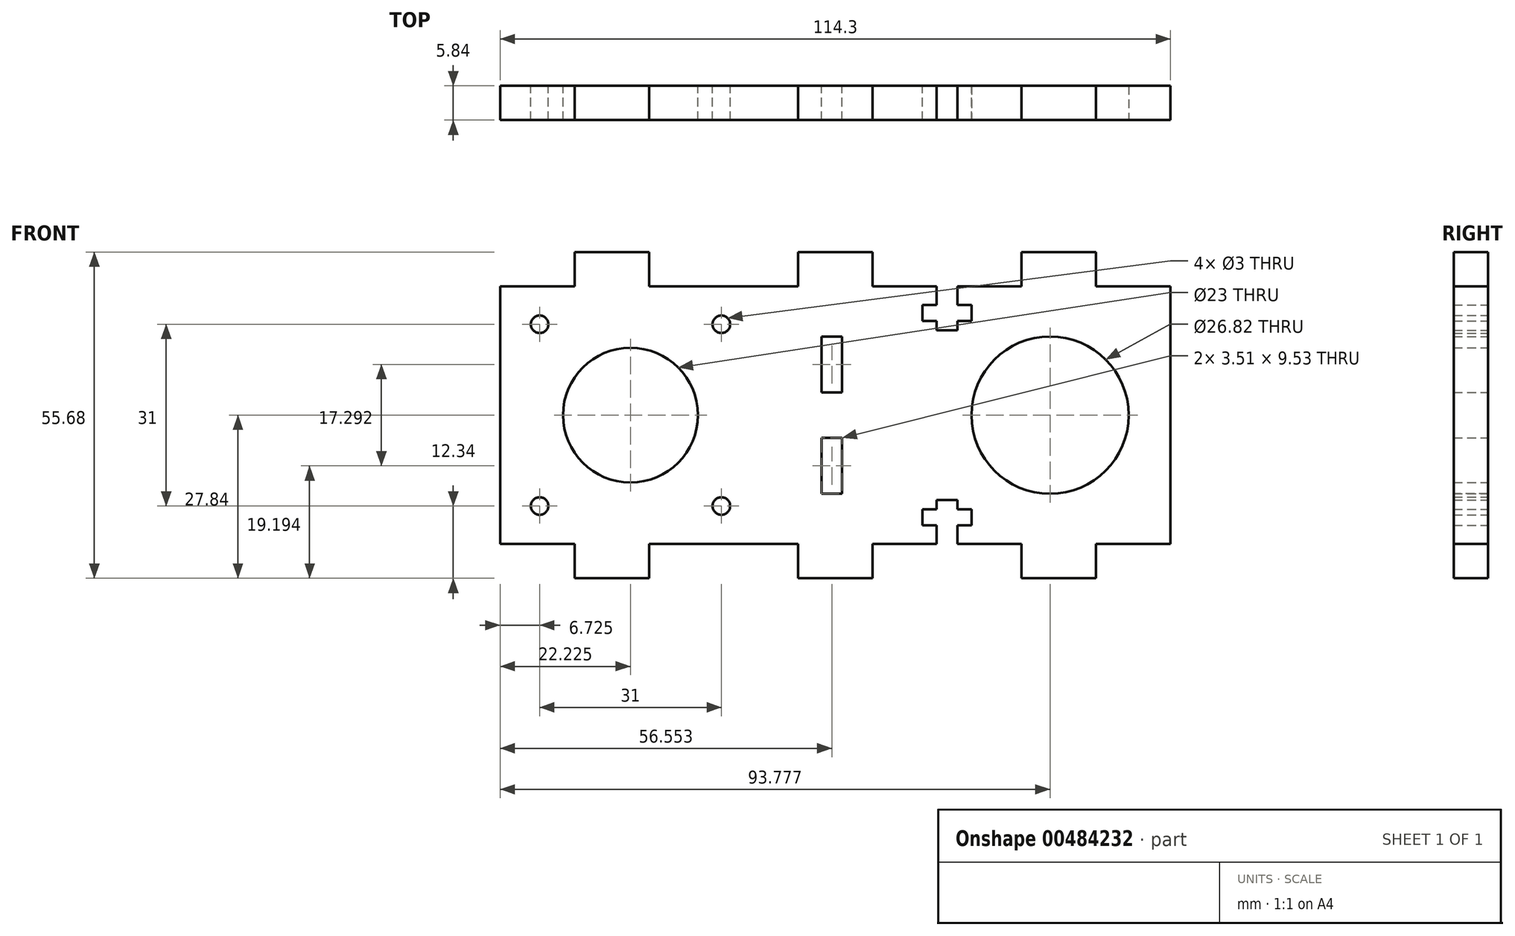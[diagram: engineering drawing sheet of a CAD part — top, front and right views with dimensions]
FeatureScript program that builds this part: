
annotation { "Feature Type Name" : "Feature", "Feature Type Description" : "" }
export const myFeature = defineFeature(function(context is Context, id is Id, definition is map)
    precondition{}
    {
        {
            var Q0;
            Q0=qCreatedBy(makeId("Front.planeOp"),FACE);
            var sketch = newSketch(context, id + "F0", { "sketchPlane" : qUnion([Q0])});
            skLineSegment(sketch, "E0.bottom", {"start": v(-57.15, 22) * mm, "end": v(-44.45, 22) * mm});
            skLineSegment(sketch, "E0.left", {"start": v(-57.15, 22) * mm, "end": v(-57.15, -22) * mm});
            skLineSegment(sketch, "E0.right", {"start": v(57.15, 22) * mm, "end": v(57.15, -22) * mm});
            skPoint(sketch, "E0.middle", {"position": v(0, 0) * mm});
            skCircle(sketch, "E1", {"center": v(-34.93, 0) * mm, "radius": 11.5 * mm});
            skCircle(sketch, "E2", {"center": v(36.63, 0) * mm, "radius": 10.86 * mm});
            skCircle(sketch, "E3", {"center": v(-50.43, 15.5) * mm, "radius": 1.5 * mm});
            skLineSegment(sketch, "E4", {"start": v(-34.93, 0) * mm, "end": v(-34.93, 11.5) * mm, "construction": true});
            skLineSegment(sketch, "E5", {"start": v(-34.93, 0) * mm, "end": v(-46.43, 0) * mm, "construction": true});
            skCircle(sketch, "E6.MirrorC", {"center": v(-19.43, 15.5) * mm, "radius": 1.5 * mm});
            skCircle(sketch, "E7.MirrorC", {"center": v(-19.43, -15.5) * mm, "radius": 1.5 * mm});
            skCircle(sketch, "E8.MirrorC", {"center": v(-50.43, -15.5) * mm, "radius": 1.5 * mm});
            skCircle(sketch, "E9", {"center": v(-34.93, 0) * mm, "radius": 5 * mm, "construction": true});
            skCircle(sketch, "E10", {"center": v(36.63, 0) * mm, "radius": 12.5 * mm, "construction": true});
            skLineSegment(sketch, "E11", {"start": v(-35.45, 4.97) * mm, "end": v(35.32, 12.43) * mm, "construction": true});
            skLineSegment(sketch, "E12.MirrorCS", {"start": v(-35.45, -4.97) * mm, "end": v(35.32, -12.43) * mm, "construction": true});
            skLineSegment(sketch, "E13", {"start": v(-0.6, 0) * mm, "end": v(-0.6, 12.84) * mm, "construction": true});
            skLineSegment(sketch, "E14.bottom", {"start": v(1.16, 13.4) * mm, "end": v(-2.35, 13.4) * mm});
            skLineSegment(sketch, "E14.top", {"start": v(1.16, 3.88) * mm, "end": v(-2.35, 3.88) * mm});
            skLineSegment(sketch, "E14.left", {"start": v(1.16, 13.4) * mm, "end": v(1.16, 3.88) * mm});
            skLineSegment(sketch, "E14.right", {"start": v(-2.35, 13.4) * mm, "end": v(-2.35, 3.88) * mm});
            skPoint(sketch, "E14.middle", {"position": v(-0.6, 8.65) * mm});
            skLineSegment(sketch, "E15.MirrorCS", {"start": v(1.16, -13.4) * mm, "end": v(-2.35, -13.4) * mm});
            skPoint(sketch, "E16.MirrorP", {"position": v(-0.6, -8.65) * mm});
            skLineSegment(sketch, "E17.MirrorCS", {"start": v(1.16, -13.4) * mm, "end": v(1.16, -3.88) * mm});
            skLineSegment(sketch, "E18.MirrorCS", {"start": v(1.16, -3.88) * mm, "end": v(-2.35, -3.88) * mm});
            skLineSegment(sketch, "E19.MirrorCS", {"start": v(-2.35, -13.4) * mm, "end": v(-2.35, -3.88) * mm});
            skLineSegment(sketch, "E20.top", {"start": v(-44.45, 27.84) * mm, "end": v(-31.75, 27.84) * mm});
            skLineSegment(sketch, "E20.left", {"start": v(-44.45, 22) * mm, "end": v(-44.45, 27.84) * mm});
            skLineSegment(sketch, "E20.right", {"start": v(-31.75, 22) * mm, "end": v(-31.75, 27.84) * mm});
            skPoint(sketch, "E20.middle", {"position": v(-38.1, 24.92) * mm});
            skLineSegment(sketch, "E21.trimOffspring", {"start": v(-31.75, 22) * mm, "end": v(-20.8, 22) * mm});
            skLineSegment(sketch, "E22.MirrorCS", {"start": v(44.45, 27.84) * mm, "end": v(31.75, 27.84) * mm});
            skLineSegment(sketch, "E23.MirrorCS", {"start": v(31.75, 22) * mm, "end": v(31.75, 27.84) * mm});
            skLineSegment(sketch, "E24.MirrorCS", {"start": v(44.45, 22) * mm, "end": v(44.45, 27.84) * mm});
            skPoint(sketch, "E25.MirrorP", {"position": v(38.1, 24.92) * mm});
            skLineSegment(sketch, "E26.MirrorCS", {"start": v(44.45, -22) * mm, "end": v(44.45, -27.84) * mm});
            skLineSegment(sketch, "E27.MirrorCS", {"start": v(-44.45, -27.84) * mm, "end": v(-31.75, -27.84) * mm});
            skLineSegment(sketch, "E28.MirrorCS", {"start": v(31.75, -22) * mm, "end": v(31.75, -27.84) * mm});
            skPoint(sketch, "E29.MirrorP", {"position": v(38.1, -24.92) * mm});
            skLineSegment(sketch, "E30.MirrorCS", {"start": v(44.45, -27.84) * mm, "end": v(31.75, -27.84) * mm});
            skPoint(sketch, "E31.MirrorP", {"position": v(-38.1, -24.92) * mm});
            skLineSegment(sketch, "E32.MirrorCS", {"start": v(-31.75, -22) * mm, "end": v(-31.75, -27.84) * mm});
            skLineSegment(sketch, "E33.MirrorCS", {"start": v(-44.45, -22) * mm, "end": v(-44.45, -27.84) * mm});
            skLineSegment(sketch, "E34.trimOffspring", {"start": v(-31.75, -22) * mm, "end": v(-20.8, -22) * mm});
            skLineSegment(sketch, "E35.trimOffspring", {"start": v(44.45, -22) * mm, "end": v(57.15, -22) * mm});
            skLineSegment(sketch, "E36.trimOffspring", {"start": v(44.45, 22) * mm, "end": v(57.15, 22) * mm});
            skLineSegment(sketch, "E37", {"start": v(-57.15, -22) * mm, "end": v(-44.45, -22) * mm});
            skLineSegment(sketch, "E38.top", {"start": v(-6.35, 27.84) * mm, "end": v(6.35, 27.84) * mm});
            skLineSegment(sketch, "E38.left", {"start": v(-6.35, 22) * mm, "end": v(-6.35, 27.84) * mm});
            skLineSegment(sketch, "E38.right", {"start": v(6.35, 22) * mm, "end": v(6.35, 27.84) * mm});
            skPoint(sketch, "E38.middle", {"position": v(0, 24.92) * mm});
            skLineSegment(sketch, "E39.trimOffspring", {"start": v(6.35, 22) * mm, "end": v(17.3, 22) * mm});
            skLineSegment(sketch, "E40.MirrorCS", {"start": v(6.35, -22) * mm, "end": v(6.35, -27.84) * mm});
            skPoint(sketch, "E41.MirrorP", {"position": v(0, -24.92) * mm});
            skLineSegment(sketch, "E42.MirrorCS", {"start": v(-6.35, -22) * mm, "end": v(-6.35, -27.84) * mm});
            skLineSegment(sketch, "E43.MirrorCS", {"start": v(-6.35, -27.84) * mm, "end": v(6.35, -27.84) * mm});
            skLineSegment(sketch, "E44.trimOffspring", {"start": v(6.35, -22) * mm, "end": v(17.3, -22) * mm});
            skLineSegment(sketch, "E45", {"start": v(-19.05, 22) * mm, "end": v(-19.05, -22) * mm, "construction": true});
            skPoint(sketch, "E46.middle", {"position": v(-19.05, -20.41) * mm});
            skPoint(sketch, "E47.middle", {"position": v(-19.05, -17.44) * mm});
            skPoint(sketch, "E48.middle", {"position": v(-19.05, -15.25) * mm});
            skLineSegment(sketch, "E49", {"start": v(-20.82, -16.05) * mm, "end": v(-20.8, -16.05) * mm});
            skLineSegment(sketch, "E50.trimOffspring", {"start": v(-17.3, -22) * mm, "end": v(-6.35, -22) * mm});
            skPoint(sketch, "E51.MirrorP", {"position": v(19.05, -15.25) * mm});
            skLineSegment(sketch, "E52.MirrorCS", {"start": v(17.3, -16.05) * mm, "end": v(17.3, -14.46) * mm});
            skLineSegment(sketch, "E53.MirrorCS", {"start": v(23.22, -18.83) * mm, "end": v(20.8, -18.83) * mm});
            skLineSegment(sketch, "E54.MirrorCS", {"start": v(17.3, -16.05) * mm, "end": v(14.88, -16.05) * mm});
            skLineSegment(sketch, "E55.MirrorCS", {"start": v(14.88, -18.83) * mm, "end": v(14.88, -16.05) * mm});
            skPoint(sketch, "E56.MirrorP", {"position": v(19.05, -17.44) * mm});
            skPoint(sketch, "E57.MirrorP", {"position": v(19.05, -20.41) * mm});
            skLineSegment(sketch, "E58.MirrorCS", {"start": v(20.8, -16.05) * mm, "end": v(20.8, -14.46) * mm});
            skLineSegment(sketch, "E59.MirrorCS", {"start": v(23.22, -18.83) * mm, "end": v(23.22, -16.05) * mm});
            skLineSegment(sketch, "E60.MirrorCS", {"start": v(23.22, -16.05) * mm, "end": v(20.8, -16.05) * mm});
            skLineSegment(sketch, "E61.MirrorCS", {"start": v(20.8, -14.46) * mm, "end": v(17.3, -14.46) * mm});
            skLineSegment(sketch, "E62.MirrorCS", {"start": v(20.8, -22) * mm, "end": v(20.8, -18.83) * mm});
            skLineSegment(sketch, "E63.MirrorCS", {"start": v(17.3, -18.83) * mm, "end": v(14.88, -18.83) * mm});
            skLineSegment(sketch, "E64.MirrorCS", {"start": v(17.3, -22) * mm, "end": v(17.3, -18.83) * mm});
            skLineSegment(sketch, "E65.trimOffspring", {"start": v(20.8, -22) * mm, "end": v(31.75, -22) * mm});
            skLineSegment(sketch, "E66.MirrorCS", {"start": v(23.22, 16.05) * mm, "end": v(20.8, 16.05) * mm});
            skLineSegment(sketch, "E67.MirrorCS", {"start": v(17.3, 18.83) * mm, "end": v(14.88, 18.83) * mm});
            skLineSegment(sketch, "E68.MirrorCS", {"start": v(23.22, 18.83) * mm, "end": v(20.8, 18.83) * mm});
            skLineSegment(sketch, "E69.MirrorCS", {"start": v(17.3, 16.05) * mm, "end": v(17.3, 14.46) * mm});
            skLineSegment(sketch, "E70.MirrorCS", {"start": v(17.3, 16.05) * mm, "end": v(14.88, 16.05) * mm});
            skLineSegment(sketch, "E71.MirrorCS", {"start": v(20.8, 16.05) * mm, "end": v(20.8, 14.46) * mm});
            skLineSegment(sketch, "E72.MirrorCS", {"start": v(-20.82, 16.05) * mm, "end": v(-20.8, 16.05) * mm});
            skLineSegment(sketch, "E73.MirrorCS", {"start": v(20.8, 14.46) * mm, "end": v(17.3, 14.46) * mm});
            skPoint(sketch, "E74.MirrorP", {"position": v(19.05, 20.41) * mm});
            skLineSegment(sketch, "E75.MirrorCS", {"start": v(14.88, 18.83) * mm, "end": v(14.88, 16.05) * mm});
            skPoint(sketch, "E76.MirrorP", {"position": v(-19.05, 20.41) * mm});
            skLineSegment(sketch, "E77.MirrorCS", {"start": v(23.22, 18.83) * mm, "end": v(23.22, 16.05) * mm});
            skLineSegment(sketch, "E78.MirrorCS", {"start": v(-17.3, 22) * mm, "end": v(-6.35, 22) * mm});
            skLineSegment(sketch, "E79.MirrorCS", {"start": v(20.8, 22) * mm, "end": v(20.8, 18.83) * mm});
            skPoint(sketch, "E80.MirrorP", {"position": v(19.05, 15.25) * mm});
            skLineSegment(sketch, "E81.MirrorCS", {"start": v(17.3, 22) * mm, "end": v(17.3, 18.83) * mm});
            skPoint(sketch, "E82.MirrorP", {"position": v(-19.05, 15.25) * mm});
            skPoint(sketch, "E83.MirrorP", {"position": v(-19.05, 17.44) * mm});
            skPoint(sketch, "E84.MirrorP", {"position": v(19.05, 17.44) * mm});
            skLineSegment(sketch, "E85.trimOffspring", {"start": v(20.8, 22) * mm, "end": v(31.75, 22) * mm});
            skLineSegment(sketch, "E86", {"start": v(-20.8, -22) * mm, "end": v(-17.3, -22) * mm});
            skLineSegment(sketch, "E87", {"start": v(-20.8, 22) * mm, "end": v(-17.3, 22) * mm});
            skPoint(sketch, "E88.orphan", {"position": v(-20.8, 14.46) * mm});
            skPoint(sketch, "E89.MirrorCS.end.orphan", {"position": v(-23.22, 16.05) * mm});
            skPoint(sketch, "E90.MirrorCS.end.orphan", {"position": v(-20.8, 18.83) * mm});
            skPoint(sketch, "E90.MirrorCS.start.orphan", {"position": v(-23.22, 18.83) * mm});
            skPoint(sketch, "E91.MirrorCS.start.orphan", {"position": v(-17.3, 18.83) * mm});
            skPoint(sketch, "E92.MirrorCS.start.orphan", {"position": v(-14.88, 18.83) * mm});
            skPoint(sketch, "E93.MirrorCS.end.orphan", {"position": v(-14.88, 16.05) * mm});
            skPoint(sketch, "E94.MirrorCS.end.orphan", {"position": v(-17.3, 14.46) * mm});
            skPoint(sketch, "E94.MirrorCS.start.orphan", {"position": v(-17.3, 16.05) * mm});
            skPoint(sketch, "E95.orphan", {"position": v(-20.8, -14.46) * mm});
            skPoint(sketch, "E48.right.end.orphan", {"position": v(-17.3, -14.46) * mm});
            skPoint(sketch, "E96.trimOffspring.start.orphan", {"position": v(-17.3, -16.05) * mm});
            skPoint(sketch, "E47.right.end.orphan", {"position": v(-14.88, -16.05) * mm});
            skPoint(sketch, "E97.trimOffspring.end.orphan", {"position": v(-14.88, -18.83) * mm});
            skPoint(sketch, "E46.right.end.orphan", {"position": v(-17.3, -18.83) * mm});
            skPoint(sketch, "E98.end.orphan", {"position": v(-20.8, -18.83) * mm});
            skPoint(sketch, "E47.left.start.orphan", {"position": v(-23.22, -18.83) * mm});
            skPoint(sketch, "E99.orphan", {"position": v(-23.22, -16.05) * mm});
            skSolve(sketch);
        }
        {
            var Q0;
            Q0=qSketchRegion(id+"F0",true);
            extrude(context, id + "F1", {"entities" : qUnion([Q0]), "depth" : 5.84 * mm});
        }
        {
            var Q0;
            Q0=makeQuery(id+"F1.opExtrude","CAP_FACE",FACE,{"disambiguationData":[OSD([sQuery(id+"F0.wireOp",EDGE,"E0.bottom"),sQuery(id+"F0.wireOp",EDGE,"E0.left"),sQuery(id+"F0.wireOp",EDGE,"E0.right"),sQuery(id+"F0.wireOp",EDGE,"E1"),sQuery(id+"F0.wireOp",EDGE,"E2"),sQuery(id+"F0.wireOp",EDGE,"E3"),sQuery(id+"F0.wireOp",EDGE,"E7.MirrorC"),sQuery(id+"F0.wireOp",EDGE,"E8.MirrorC"),sQuery(id+"F0.wireOp",EDGE,"E14.top"),sQuery(id+"F0.wireOp",EDGE,"E14.left"),sQuery(id+"F0.wireOp",EDGE,"E14.right"),sQuery(id+"F0.wireOp",EDGE,"E15.MirrorCS"),sQuery(id+"F0.wireOp",EDGE,"E17.MirrorCS"),sQuery(id+"F0.wireOp",EDGE,"E18.MirrorCS"),sQuery(id+"F0.wireOp",EDGE,"E19.MirrorCS"),sQuery(id+"F0.wireOp",EDGE,"E20.top"),sQuery(id+"F0.wireOp",EDGE,"E20.left"),sQuery(id+"F0.wireOp",EDGE,"E20.right"),sQuery(id+"F0.wireOp",EDGE,"E21.trimOffspring"),sQuery(id+"F0.wireOp",EDGE,"E22.MirrorCS"),sQuery(id+"F0.wireOp",EDGE,"E23.MirrorCS"),sQuery(id+"F0.wireOp",EDGE,"E24.MirrorCS"),sQuery(id+"F0.wireOp",EDGE,"E26.MirrorCS"),sQuery(id+"F0.wireOp",EDGE,"E27.MirrorCS"),sQuery(id+"F0.wireOp",EDGE,"E28.MirrorCS"),sQuery(id+"F0.wireOp",EDGE,"E30.MirrorCS"),sQuery(id+"F0.wireOp",EDGE,"E32.MirrorCS"),sQuery(id+"F0.wireOp",EDGE,"E33.MirrorCS"),sQuery(id+"F0.wireOp",EDGE,"E34.trimOffspring"),sQuery(id+"F0.wireOp",EDGE,"E35.trimOffspring"),sQuery(id+"F0.wireOp",EDGE,"E36.trimOffspring"),sQuery(id+"F0.wireOp",EDGE,"E37"),sQuery(id+"F0.wireOp",EDGE,"E38.top"),sQuery(id+"F0.wireOp",EDGE,"E38.left"),sQuery(id+"F0.wireOp",EDGE,"E38.right"),sQuery(id+"F0.wireOp",EDGE,"E40.MirrorCS"),sQuery(id+"F0.wireOp",EDGE,"E42.MirrorCS"),sQuery(id+"F0.wireOp",EDGE,"E43.MirrorCS"),sQuery(id+"F0.wireOp",EDGE,"E44.trimOffspring"),sQuery(id+"F0.wireOp",EDGE,"E50.trimOffspring"),sQuery(id+"F0.wireOp",EDGE,"E52.MirrorCS"),sQuery(id+"F0.wireOp",EDGE,"E53.MirrorCS"),sQuery(id+"F0.wireOp",EDGE,"E54.MirrorCS"),sQuery(id+"F0.wireOp",EDGE,"E55.MirrorCS"),sQuery(id+"F0.wireOp",EDGE,"E58.MirrorCS"),sQuery(id+"F0.wireOp",EDGE,"E59.MirrorCS"),sQuery(id+"F0.wireOp",EDGE,"E60.MirrorCS"),sQuery(id+"F0.wireOp",EDGE,"E61.MirrorCS"),sQuery(id+"F0.wireOp",EDGE,"E62.MirrorCS"),sQuery(id+"F0.wireOp",EDGE,"E63.MirrorCS"),sQuery(id+"F0.wireOp",EDGE,"E64.MirrorCS"),sQuery(id+"F0.wireOp",EDGE,"E65.trimOffspring"),sQuery(id+"F0.wireOp",EDGE,"E66.MirrorCS"),sQuery(id+"F0.wireOp",EDGE,"E67.MirrorCS"),sQuery(id+"F0.wireOp",EDGE,"E68.MirrorCS"),sQuery(id+"F0.wireOp",EDGE,"E69.MirrorCS"),sQuery(id+"F0.wireOp",EDGE,"E70.MirrorCS"),sQuery(id+"F0.wireOp",EDGE,"E71.MirrorCS"),sQuery(id+"F0.wireOp",EDGE,"E73.MirrorCS"),sQuery(id+"F0.wireOp",EDGE,"E14.bottom"),sQuery(id+"F0.wireOp",EDGE,"E39.trimOffspring"),sQuery(id+"F0.wireOp",EDGE,"E75.MirrorCS"),sQuery(id+"F0.wireOp",EDGE,"E77.MirrorCS"),sQuery(id+"F0.wireOp",EDGE,"E6.MirrorC"),sQuery(id+"F0.wireOp",EDGE,"E79.MirrorCS"),sQuery(id+"F0.wireOp",EDGE,"E81.MirrorCS"),sQuery(id+"F0.wireOp",EDGE,"E78.MirrorCS"),sQuery(id+"F0.wireOp",EDGE,"E85.trimOffspring"),sQuery(id+"F0.wireOp",EDGE,"E86"),sQuery(id+"F0.wireOp",EDGE,"E87")])],"isStart":false});
            var sketch = newSketch(context, id + "F2", { "sketchPlane" : qUnion([Q0])});
            skCircle(sketch, "E100", {"center": v(36.63, 0) * mm, "radius": 13.4 * mm});
            skSolve(sketch);
        }
        {
            var Q0;
            Q0 = qSketchRegion(id + "F2", true);
            extrude(context, id + "F3", {"entities" : qUnion([Q0]), "operationType" : NewBodyOperationType.REMOVE, "oppositeDirection" : true, "depth" : 25.4 * mm});
        }
    });
